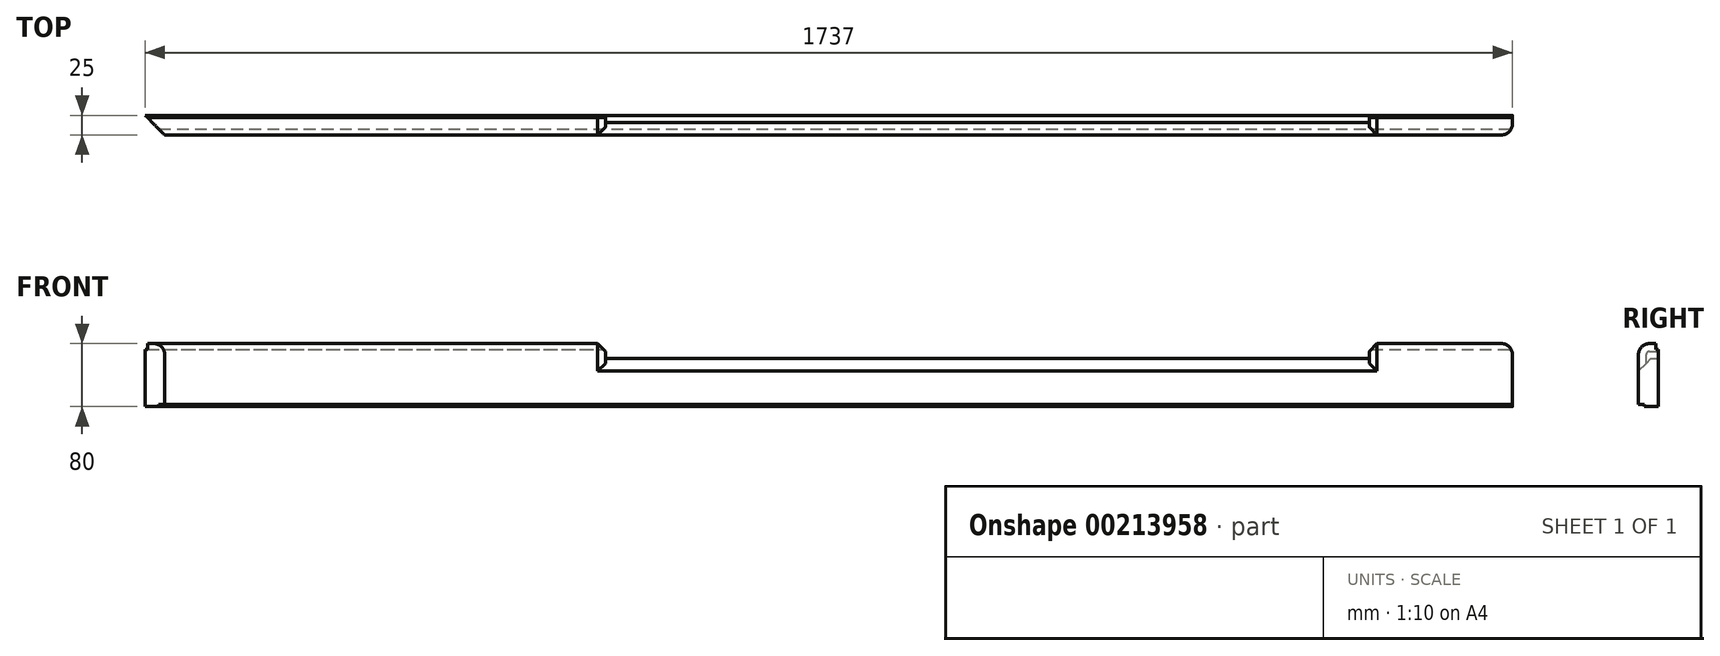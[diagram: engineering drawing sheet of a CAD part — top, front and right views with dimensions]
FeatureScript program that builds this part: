
annotation { "Feature Type Name" : "Feature", "Feature Type Description" : "" }
export const myFeature = defineFeature(function(context is Context, id is Id, definition is map)
    precondition{}
    {
        {
            var Q0;
            Q0=qCreatedBy(makeId("Front.planeOp"),FACE);
            var sketch = newSketch(context, id + "F0", { "sketchPlane" : qUnion([Q0])});
            skLineSegment(sketch, "E0.bottom", {"start": v(0, 259.74) * mm, "end": v(1737, 259.74) * mm});
            skLineSegment(sketch, "E0.top", {"start": v(0, 339.74) * mm, "end": v(585, 339.74) * mm});
            skLineSegment(sketch, "E0.left", {"start": v(0, 259.74) * mm, "end": v(0, 339.74) * mm});
            skLineSegment(sketch, "E0.right", {"start": v(1737, 259.74) * mm, "end": v(1737, 339.74) * mm});
            skLineSegment(sketch, "E1.top", {"start": v(585, 320.74) * mm, "end": v(1555, 320.74) * mm});
            skLineSegment(sketch, "E1.left", {"start": v(585, 339.74) * mm, "end": v(585, 320.74) * mm});
            skLineSegment(sketch, "E1.right", {"start": v(1555, 339.74) * mm, "end": v(1555, 320.74) * mm});
            skLineSegment(sketch, "E2.trimOffspring", {"start": v(1555, 339.74) * mm, "end": v(1737, 339.74) * mm});
            skSolve(sketch);
        }
        {
            var Q0;
            Q0 = qSketchRegion(id + "F0", true);
            extrude(context, id + "F1", {"entities" : qUnion([Q0]), "depth" : 25 * mm});
        }
        {
            var Q0;
            Q0=makeQuery(id+"F1.opExtrude","SWEPT_FACE",FACE,{"disambiguationData":[OSD([sQuery(id+"F0.wireOp",EDGE,"E0.right")])]});
            var sketch = newSketch(context, id + "F2", { "sketchPlane" : qUnion([Q0])});
            skLineSegment(sketch, "E3.bottom", {"start": v(-34.35, 262.74) * mm, "end": v(-17.5, 262.74) * mm});
            skLineSegment(sketch, "E3.top", {"start": v(-34.35, 252.3) * mm, "end": v(-17.5, 252.3) * mm});
            skLineSegment(sketch, "E3.left", {"start": v(-34.35, 262.74) * mm, "end": v(-34.35, 252.3) * mm});
            skLineSegment(sketch, "E3.right", {"start": v(-17.5, 262.74) * mm, "end": v(-17.5, 252.3) * mm});
            skLineSegment(sketch, "E4.bottom", {"start": v(-3, 342) * mm, "end": v(2.89, 342) * mm});
            skLineSegment(sketch, "E4.top", {"start": v(-3, 332.24) * mm, "end": v(2.89, 332.24) * mm});
            skLineSegment(sketch, "E4.left", {"start": v(-3, 342) * mm, "end": v(-3, 332.24) * mm});
            skLineSegment(sketch, "E4.right", {"start": v(2.89, 342) * mm, "end": v(2.89, 332.24) * mm});
            skPoint(sketch, "E5.right.end.orphan", {"position": v(-34.35, 354.26) * mm});
            skPoint(sketch, "E5.left.start.orphan", {"position": v(0, 344.28) * mm});
            skSolve(sketch);
        }
        {
            var Q0;
            Q0 = qSketchRegion(id + "F2", true);
            extrude(context, id + "F3", {"entities" : qUnion([Q0]), "operationType" : NewBodyOperationType.REMOVE, "endBound" : BoundingType.THROUGH_ALL, "oppositeDirection" : true, "depth" : 25 * mm});
        }
        {
            var Q0;
            Q0=makeQuery(id+"F1.opExtrude","SWEPT_FACE",FACE,{"disambiguationData":[OSD([sQuery(id+"F0.wireOp",EDGE,"E0.top")])]});
            var sketch = newSketch(context, id + "F4", { "sketchPlane" : qUnion([Q0])});
            skLineSegment(sketch, "E6", {"start": v(0, 0) * mm, "end": v(29.03, -29.03) * mm});
            skLineSegment(sketch, "E7", {"start": v(29.03, -29.03) * mm, "end": v(-6.03, -29.03) * mm});
            skLineSegment(sketch, "E8", {"start": v(-6.03, -29.03) * mm, "end": v(-6.03, 0) * mm});
            skLineSegment(sketch, "E9", {"start": v(-6.03, 0) * mm, "end": v(0, 0) * mm});
            skSolve(sketch);
        }
        {
            var Q0;
            Q0 = qSketchRegion(id + "F4", true);
            extrude(context, id + "F5", {"entities" : qUnion([Q0]), "operationType" : NewBodyOperationType.REMOVE, "endBound" : BoundingType.THROUGH_ALL, "oppositeDirection" : true, "depth" : 25 * mm});
        }
        {
            var Q0;
            Q0=makeQuery(id+"F1.opExtrude","CAP_EDGE",EDGE,{"disambiguationData":[OSD([sQuery(id+"F0.wireOp",EDGE,"E0.top")])],"isStart":false});
            var Q1;
            Q1=makeQuery(id+"F1.opExtrude","CAP_EDGE",EDGE,{"disambiguationData":[OSD([sQuery(id+"F0.wireOp",EDGE,"E2.trimOffspring")])],"isStart":false});
            fillet(context, id + "F6", {"entities" : qUnion([Q0, Q1]), "radius" : 14 * mm, "tangentPropagation" : true, "allowEdgeOverflow" : false});
        }
        {
            var Q0;
            Q0=makeQuery(id+"F1.opExtrude","CAP_EDGE",EDGE,{"disambiguationData":[OSD([sQuery(id+"F0.wireOp",EDGE,"E0.right")])],"isStart":false});
            fillet(context, id + "F7", {"entities" : qUnion([Q0]), "radius" : 14 * mm, "tangentPropagation" : true, "allowEdgeOverflow" : false});
        }
        {
            var Q0;
            Q0=makeQuery(id+"F1.opExtrude","CAP_EDGE",EDGE,{"disambiguationData":[OSD([sQuery(id+"F0.wireOp",EDGE,"E1.top")])],"isStart":false});
            chamfer(context, id + "F8", {"entities" : qUnion([Q0]), "width" : 16 * mm, "tangentPropagation" : true});
        }
        {
            var Q0;
            Q0=makeQuery(id+"F1.opExtrude","CAP_EDGE",EDGE,{"disambiguationData":[OSD([sQuery(id+"F0.wireOp",EDGE,"E1.left")])],"isStart":false});
            var Q1;
            Q1=makeQuery(id+"F1.opExtrude","CAP_EDGE",EDGE,{"disambiguationData":[OSD([sQuery(id+"F0.wireOp",EDGE,"E1.right")])],"isStart":false});
            chamfer(context, id + "F9", {"entities" : qUnion([Q0, Q1]), "width" : 10 * mm, "tangentPropagation" : true});
        }
    });
